# Revit family: 57690 Varionaut 150
name_source: partatom
category: Körper
revit_build: Autodesk Revit 2015 (Build: 20140606_1530(x64)
units: mm (PartAtom-declared; Revit-internal decimal feet)

## types (1)
- 57690_Varionaut 150 /DMX/02
    Beschreibung = controllable pump
    Dimensionsincl incl. filter LxWxH = 12.2x6.3x6.2
    Dynamic behaviour speed/ time to reach full fountain height from 0 - 100% with comet 5-8 = 1 s
    Environmental conditions, dry application = Ambient temperature max. 30°C with natural convection, max. 40°C with forced convection, no direct sun exposure permitted
    Environmental conditions, submersible application = Water temperature min. 4°C to max. 35°C
    Filter housing = Plastic / stainless steel
    Filter surface = 0.24 sq.ft
    H max = 18.37 ft
    Hersteller = OASE GmbH Post Box 2069, 48469 Hörstel , Germany +49 5454 80-0
    Homepage = http://www.oase-livingwater.com
    Immersion depth max. = 13.1 ft
    Input DMX = 3.28 ft. BUS cable with DMX box
    Input power = 20 ft power cable without plug (R&D)
    Max. powering up / min. Off time = 1 x per minute / 10 s
    Modell = Varionaut 150 /DMX/02
    MotorType / Electronic = 24 V DC EC-Motor, DMX controlled (DMX-RDM enabled)
    Name = Varionaut 150 /DMX/02
    Norminal voltage = 220-240,50/50 V/Hz
    Number of BMX chanels = 2 channels (control channel, speed channel)
    Order no. = 57690
    Pressure side connection = 1 1/2 inch
    Protection class = IP 68
    Pump housing = Plastic
    Q max = 2377 gph
    Qmin Offset-Modus - DMX 0 = 380.4 gph
    Suction side connection = 1 1/2 inch
    Vorgabe-Ansicht = 1219 mm
    Weight = 11 lb
    power max. = 130 W

## geometry (parser evidence)
native form markers: Blend x6
no freeform markers — native parametric forms only
